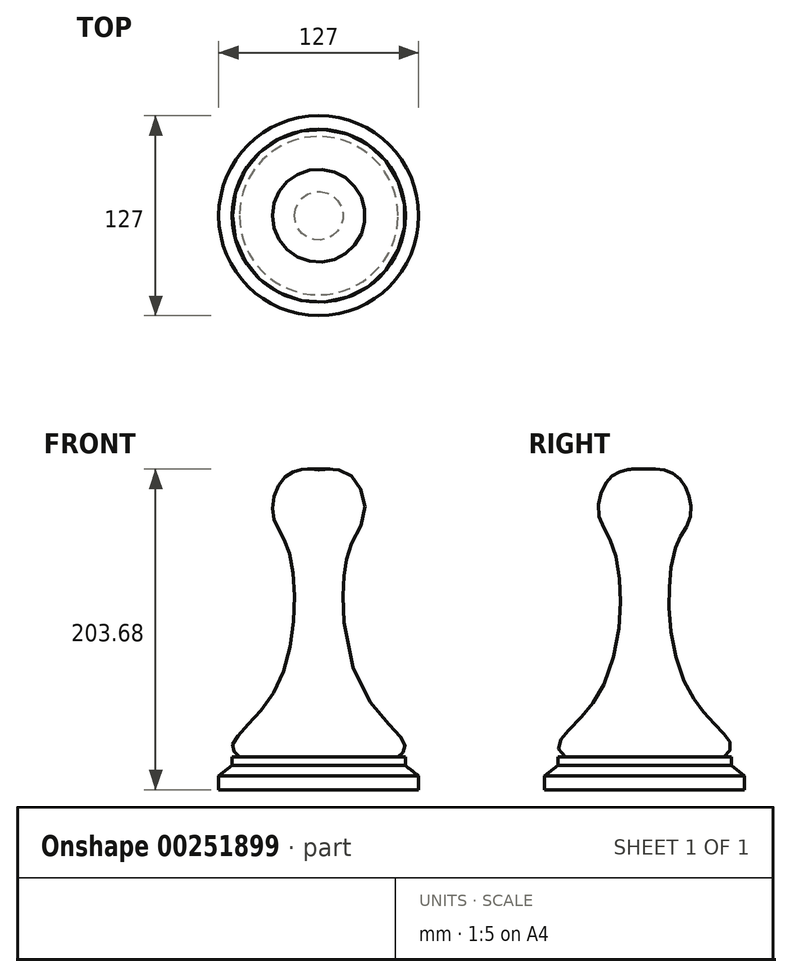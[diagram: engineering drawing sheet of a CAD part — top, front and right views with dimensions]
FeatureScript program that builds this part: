
annotation { "Feature Type Name" : "Feature", "Feature Type Description" : "" }
export const myFeature = defineFeature(function(context is Context, id is Id, definition is map)
    precondition{}
    {
        {
            var Q0;
            Q0=qCreatedBy(makeId("Front.planeOp"),FACE);
            var sketch = newSketch(context, id + "F0", { "sketchPlane" : qUnion([Q0])});
            skLineSegment(sketch, "E0", {"start": v(0, 107.23) * mm, "end": v(0, -95.97) * mm, "construction": true});
            skLineSegment(sketch, "E1", {"start": v(0, -95.97) * mm, "end": v(-63.5, -95.97) * mm});
            skLineSegment(sketch, "E2", {"start": v(-63.5, -95.97) * mm, "end": v(-63.5, -87.18) * mm});
            skLineSegment(sketch, "E3", {"start": v(-63.5, -87.18) * mm, "end": v(-54.96, -80.52) * mm});
            skLineSegment(sketch, "E4", {"start": v(-54.96, -80.52) * mm, "end": v(-54.96, -75.2) * mm});
            skLineSegment(sketch, "E5", {"start": v(-54.96, -75.2) * mm, "end": v(-50.3, -75.2) * mm});
            skLineSegment(sketch, "E6", {"start": v(0, 107.23) * mm, "end": v(0, -95.97) * mm});
            skFitSpline(sketch, "E7", {"points": [v(0, 107.23) * mm, v(-12.14, 107.23) * mm, v(-24.3, 99.31) * mm, v(-29.04, 77.97) * mm, v(-19.27, 56.32) * mm, v(-27.3, -31.75) * mm, v(-54.86, -67.62) * mm, v(-50.3, -75.2) * mm], "startDerivative": vector(-124.98, 12.84) * mm, "endDerivative": vector(91.77, -82.9) * mm});
            skSolve(sketch);
        }
        {
            var Q0;
            Q0=makeQuery(id+"F0.imprint","IMPRINT",FACE,{"disambiguationData":[TD([[makeQuery(id+"F0.imprint","IMPRINT",EDGE,{"derivedFrom":sQuery(id+"F0.wireOp",EDGE,"E1")}),-1.0]])]});
            var Q1;
            Q1=sQuery(id+"F0.wireOp",EDGE,"E6");
            revolve(context, id + "F1", {"entities" : qUnion([Q0]), "axis" : qUnion([Q1]), "revolveType" : RevolveType.FULL});
        }
    });
